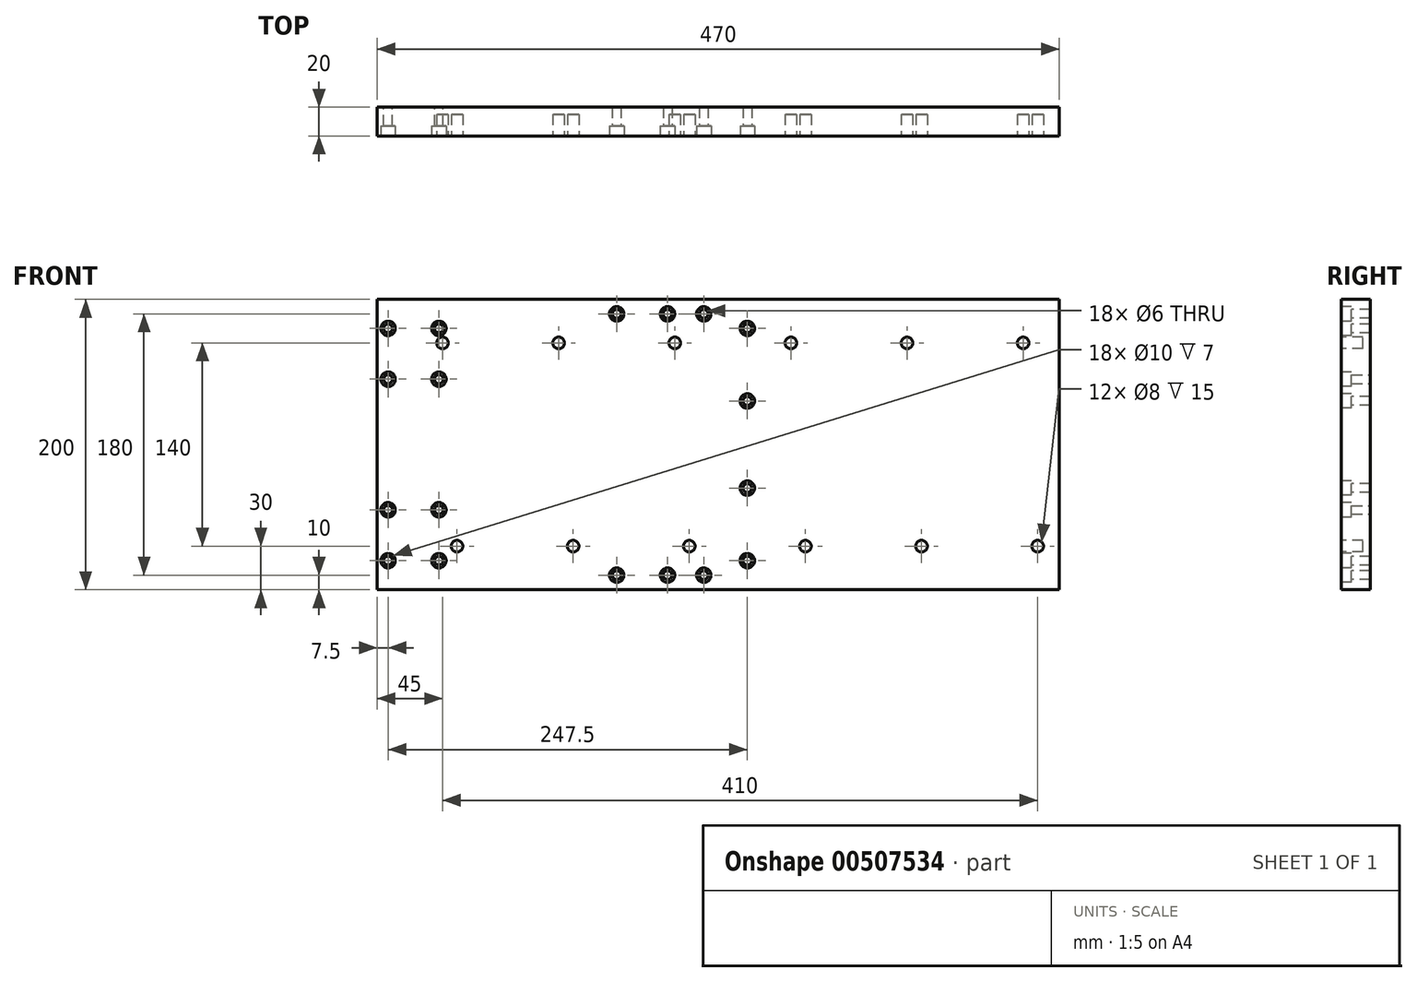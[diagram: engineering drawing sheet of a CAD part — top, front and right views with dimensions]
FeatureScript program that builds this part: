
annotation { "Feature Type Name" : "Feature", "Feature Type Description" : "" }
export const myFeature = defineFeature(function(context is Context, id is Id, definition is map)
    precondition{}
    {
        {
            var Q0;
            Q0=qCreatedBy(makeId("Front.planeOp"),FACE);
            var sketch = newSketch(context, id + "F0", { "sketchPlane" : qUnion([Q0])});
            skLineSegment(sketch, "E0.bottom", {"start": v(0, 0) * mm, "end": v(470, 0) * mm});
            skLineSegment(sketch, "E0.top", {"start": v(0, 200) * mm, "end": v(470, 200) * mm});
            skLineSegment(sketch, "E0.left", {"start": v(0, 0) * mm, "end": v(0, 200) * mm});
            skLineSegment(sketch, "E0.right", {"start": v(470, 0) * mm, "end": v(470, 200) * mm});
            skCircle(sketch, "E1", {"center": v(7.5, 20) * mm, "radius": 3 * mm});
            skCircle(sketch, "E2", {"center": v(7.5, 55) * mm, "radius": 3 * mm});
            skCircle(sketch, "E3", {"center": v(7.5, 145) * mm, "radius": 3 * mm});
            skCircle(sketch, "E4", {"center": v(7.5, 180) * mm, "radius": 3 * mm});
            skCircle(sketch, "E5", {"center": v(42.5, 20) * mm, "radius": 3 * mm});
            skCircle(sketch, "E6", {"center": v(42.5, 55) * mm, "radius": 3 * mm});
            skCircle(sketch, "E7", {"center": v(42.5, 145) * mm, "radius": 3 * mm});
            skCircle(sketch, "E8", {"center": v(42.5, 180) * mm, "radius": 3 * mm});
            skSolve(sketch);
        }
        {
            var Q0;
            Q0=makeQuery(id+"F0.imprint","IMPRINT",FACE,{"disambiguationData":[TD([[makeQuery(id+"F0.imprint","IMPRINT",EDGE,{"derivedFrom":sQuery(id+"F0.wireOp",EDGE,"E0.bottom")}),1.0]])]});
            extrude(context, id + "F1", {"entities" : qUnion([Q0]), "depth" : 20 * mm});
        }
        {
            var Q0;
            Q0=makeQuery(id+"F1.opExtrude","CAP_FACE",FACE,{"disambiguationData":[OSD([sQuery(id+"F0.wireOp",EDGE,"E0.bottom"),sQuery(id+"F0.wireOp",EDGE,"E0.top"),sQuery(id+"F0.wireOp",EDGE,"E0.left"),sQuery(id+"F0.wireOp",EDGE,"E0.right"),sQuery(id+"F0.wireOp",EDGE,"E1"),sQuery(id+"F0.wireOp",EDGE,"E2"),sQuery(id+"F0.wireOp",EDGE,"E3"),sQuery(id+"F0.wireOp",EDGE,"E4"),sQuery(id+"F0.wireOp",EDGE,"E5"),sQuery(id+"F0.wireOp",EDGE,"E6"),sQuery(id+"F0.wireOp",EDGE,"E7"),sQuery(id+"F0.wireOp",EDGE,"E8")])],"isStart":false});
            var sketch = newSketch(context, id + "F2", { "sketchPlane" : qUnion([Q0])});
            skCircle(sketch, "E9", {"center": v(7.5, 180) * mm, "radius": 5 * mm});
            skCircle(sketch, "E10", {"center": v(42.5, 180) * mm, "radius": 5 * mm});
            skCircle(sketch, "E11", {"center": v(7.5, 145) * mm, "radius": 5 * mm});
            skCircle(sketch, "E12", {"center": v(42.5, 145) * mm, "radius": 5 * mm});
            skCircle(sketch, "E13", {"center": v(7.5, 55) * mm, "radius": 5 * mm});
            skCircle(sketch, "E14", {"center": v(42.5, 55) * mm, "radius": 5 * mm});
            skCircle(sketch, "E15", {"center": v(7.5, 20) * mm, "radius": 5 * mm});
            skCircle(sketch, "E16", {"center": v(42.5, 20) * mm, "radius": 5 * mm});
            skSolve(sketch);
        }
        {
            var Q0;
            Q0=qSketchRegion(id+"F2",true);
            extrude(context, id + "F3", {"entities" : qUnion([Q0]), "operationType" : NewBodyOperationType.REMOVE, "oppositeDirection" : true, "depth" : 7 * mm});
        }
        {
            var Q0;
            Q0=makeQuery(id+"F1.opExtrude","CAP_FACE",FACE,{"disambiguationData":[OSD([sQuery(id+"F0.wireOp",EDGE,"E0.bottom"),sQuery(id+"F0.wireOp",EDGE,"E0.top"),sQuery(id+"F0.wireOp",EDGE,"E0.left"),sQuery(id+"F0.wireOp",EDGE,"E0.right"),sQuery(id+"F0.wireOp",EDGE,"E1"),sQuery(id+"F0.wireOp",EDGE,"E2"),sQuery(id+"F0.wireOp",EDGE,"E3"),sQuery(id+"F0.wireOp",EDGE,"E4"),sQuery(id+"F0.wireOp",EDGE,"E5"),sQuery(id+"F0.wireOp",EDGE,"E6"),sQuery(id+"F0.wireOp",EDGE,"E7"),sQuery(id+"F0.wireOp",EDGE,"E8")])],"isStart":false});
            var sketch = newSketch(context, id + "F4", { "sketchPlane" : qUnion([Q0])});
            skCircle(sketch, "E17", {"center": v(255, 180) * mm, "radius": 3 * mm});
            skCircle(sketch, "E18", {"center": v(255, 130) * mm, "radius": 3 * mm});
            skCircle(sketch, "E19", {"center": v(255, 70) * mm, "radius": 3 * mm});
            skCircle(sketch, "E20", {"center": v(255, 20) * mm, "radius": 3 * mm});
            skSolve(sketch);
        }
        {
            var Q0;
            Q0 = qSketchRegion(id + "F4", true);
            extrude(context, id + "F5", {"entities" : qUnion([Q0]), "operationType" : NewBodyOperationType.REMOVE, "oppositeDirection" : true, "depth" : 20 * mm});
        }
        {
            var Q0;
            Q0=makeQuery(id+"F1.opExtrude","CAP_FACE",FACE,{"disambiguationData":[OSD([sQuery(id+"F0.wireOp",EDGE,"E0.bottom"),sQuery(id+"F0.wireOp",EDGE,"E0.top"),sQuery(id+"F0.wireOp",EDGE,"E0.left"),sQuery(id+"F0.wireOp",EDGE,"E0.right"),sQuery(id+"F0.wireOp",EDGE,"E1"),sQuery(id+"F0.wireOp",EDGE,"E2"),sQuery(id+"F0.wireOp",EDGE,"E3"),sQuery(id+"F0.wireOp",EDGE,"E4"),sQuery(id+"F0.wireOp",EDGE,"E5"),sQuery(id+"F0.wireOp",EDGE,"E6"),sQuery(id+"F0.wireOp",EDGE,"E7"),sQuery(id+"F0.wireOp",EDGE,"E8")])],"isStart":false});
            var sketch = newSketch(context, id + "F6", { "sketchPlane" : qUnion([Q0])});
            skCircle(sketch, "E21", {"center": v(255, 20) * mm, "radius": 5 * mm});
            skCircle(sketch, "E22", {"center": v(255, 70) * mm, "radius": 5 * mm});
            skCircle(sketch, "E23", {"center": v(255, 130) * mm, "radius": 5 * mm});
            skCircle(sketch, "E24", {"center": v(255, 180) * mm, "radius": 5 * mm});
            skSolve(sketch);
        }
        {
            var Q0;
            Q0 = qSketchRegion(id + "F6", true);
            extrude(context, id + "F7", {"entities" : qUnion([Q0]), "operationType" : NewBodyOperationType.REMOVE, "oppositeDirection" : true, "depth" : 7 * mm});
        }
        {
            var Q0;
            Q0=makeQuery(id+"F1.opExtrude","CAP_FACE",FACE,{"disambiguationData":[OSD([sQuery(id+"F0.wireOp",EDGE,"E0.bottom"),sQuery(id+"F0.wireOp",EDGE,"E0.top"),sQuery(id+"F0.wireOp",EDGE,"E0.left"),sQuery(id+"F0.wireOp",EDGE,"E0.right"),sQuery(id+"F0.wireOp",EDGE,"E1"),sQuery(id+"F0.wireOp",EDGE,"E2"),sQuery(id+"F0.wireOp",EDGE,"E3"),sQuery(id+"F0.wireOp",EDGE,"E4"),sQuery(id+"F0.wireOp",EDGE,"E5"),sQuery(id+"F0.wireOp",EDGE,"E6"),sQuery(id+"F0.wireOp",EDGE,"E7"),sQuery(id+"F0.wireOp",EDGE,"E8")])],"isStart":false});
            var sketch = newSketch(context, id + "F8", { "sketchPlane" : qUnion([Q0])});
            skCircle(sketch, "E25", {"center": v(225, 190) * mm, "radius": 3 * mm});
            skCircle(sketch, "E26", {"center": v(200, 190) * mm, "radius": 3 * mm});
            skCircle(sketch, "E27", {"center": v(165, 190) * mm, "radius": 3 * mm});
            skCircle(sketch, "E28", {"center": v(165, 10) * mm, "radius": 3 * mm});
            skCircle(sketch, "E29", {"center": v(200, 10) * mm, "radius": 3 * mm});
            skCircle(sketch, "E30", {"center": v(225, 10) * mm, "radius": 3 * mm});
            skSolve(sketch);
        }
        {
            var Q0;
            Q0 = qSketchRegion(id + "F8", true);
            extrude(context, id + "F9", {"entities" : qUnion([Q0]), "operationType" : NewBodyOperationType.REMOVE, "oppositeDirection" : true, "depth" : 20 * mm});
        }
        {
            var Q0;
            Q0=makeQuery(id+"F1.opExtrude","CAP_FACE",FACE,{"disambiguationData":[OSD([sQuery(id+"F0.wireOp",EDGE,"E0.bottom"),sQuery(id+"F0.wireOp",EDGE,"E0.top"),sQuery(id+"F0.wireOp",EDGE,"E0.left"),sQuery(id+"F0.wireOp",EDGE,"E0.right"),sQuery(id+"F0.wireOp",EDGE,"E1"),sQuery(id+"F0.wireOp",EDGE,"E2"),sQuery(id+"F0.wireOp",EDGE,"E3"),sQuery(id+"F0.wireOp",EDGE,"E4"),sQuery(id+"F0.wireOp",EDGE,"E5"),sQuery(id+"F0.wireOp",EDGE,"E6"),sQuery(id+"F0.wireOp",EDGE,"E7"),sQuery(id+"F0.wireOp",EDGE,"E8")])],"isStart":false});
            var sketch = newSketch(context, id + "F10", { "sketchPlane" : qUnion([Q0])});
            skCircle(sketch, "E31", {"center": v(165, 190) * mm, "radius": 5 * mm});
            skCircle(sketch, "E32", {"center": v(200, 190) * mm, "radius": 5 * mm});
            skCircle(sketch, "E33", {"center": v(225, 190) * mm, "radius": 5 * mm});
            skCircle(sketch, "E34", {"center": v(165, 10) * mm, "radius": 5 * mm});
            skCircle(sketch, "E35", {"center": v(200, 10) * mm, "radius": 5 * mm});
            skCircle(sketch, "E36", {"center": v(225, 10) * mm, "radius": 5 * mm});
            skSolve(sketch);
        }
        {
            var Q0;
            Q0 = qSketchRegion(id + "F10", true);
            extrude(context, id + "F11", {"entities" : qUnion([Q0]), "operationType" : NewBodyOperationType.REMOVE, "oppositeDirection" : true, "depth" : 7 * mm});
        }
        {
            var Q0;
            Q0=makeQuery(id+"F1.opExtrude","CAP_FACE",FACE,{"disambiguationData":[OSD([sQuery(id+"F0.wireOp",EDGE,"E0.bottom"),sQuery(id+"F0.wireOp",EDGE,"E0.top"),sQuery(id+"F0.wireOp",EDGE,"E0.left"),sQuery(id+"F0.wireOp",EDGE,"E0.right"),sQuery(id+"F0.wireOp",EDGE,"E1"),sQuery(id+"F0.wireOp",EDGE,"E2"),sQuery(id+"F0.wireOp",EDGE,"E3"),sQuery(id+"F0.wireOp",EDGE,"E4"),sQuery(id+"F0.wireOp",EDGE,"E5"),sQuery(id+"F0.wireOp",EDGE,"E6"),sQuery(id+"F0.wireOp",EDGE,"E7"),sQuery(id+"F0.wireOp",EDGE,"E8")])],"isStart":false});
            var sketch = newSketch(context, id + "F12", { "sketchPlane" : qUnion([Q0])});
            skCircle(sketch, "E37", {"center": v(45, 170) * mm, "radius": 4 * mm});
            skCircle(sketch, "E38", {"center": v(125, 170) * mm, "radius": 4 * mm});
            skCircle(sketch, "E39", {"center": v(205, 170) * mm, "radius": 4 * mm});
            skCircle(sketch, "E40", {"center": v(285, 170) * mm, "radius": 4 * mm});
            skCircle(sketch, "E41", {"center": v(365, 170) * mm, "radius": 4 * mm});
            skCircle(sketch, "E42", {"center": v(445, 170) * mm, "radius": 4 * mm});
            skCircle(sketch, "E43", {"center": v(55, 30) * mm, "radius": 4 * mm});
            skCircle(sketch, "E44", {"center": v(135, 30) * mm, "radius": 4 * mm});
            skCircle(sketch, "E45", {"center": v(215, 30) * mm, "radius": 4 * mm});
            skCircle(sketch, "E46", {"center": v(295, 30) * mm, "radius": 4 * mm});
            skCircle(sketch, "E47", {"center": v(375, 30) * mm, "radius": 4 * mm});
            skCircle(sketch, "E48", {"center": v(455, 30) * mm, "radius": 4 * mm});
            skSolve(sketch);
        }
        {
            var Q0;
            Q0 = qSketchRegion(id + "F12", true);
            extrude(context, id + "F13", {"entities" : qUnion([Q0]), "operationType" : NewBodyOperationType.REMOVE, "oppositeDirection" : true, "depth" : 15 * mm});
        }
    });
